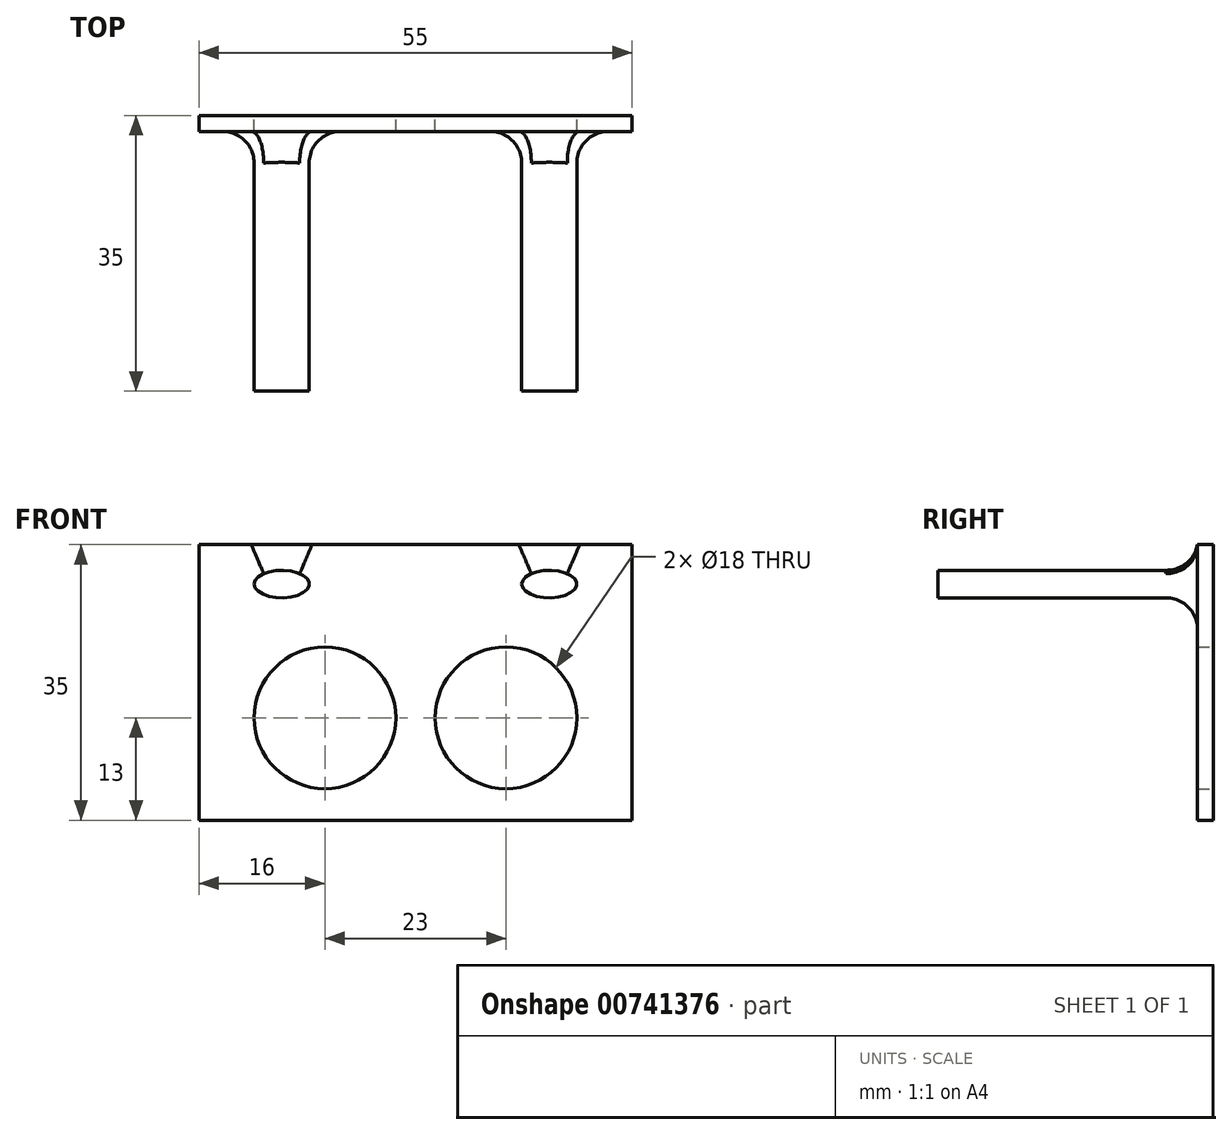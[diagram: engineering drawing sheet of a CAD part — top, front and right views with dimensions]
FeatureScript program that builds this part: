
annotation { "Feature Type Name" : "Feature", "Feature Type Description" : "" }
export const myFeature = defineFeature(function(context is Context, id is Id, definition is map)
    precondition{}
    {
        {
            var Q0;
            Q0=qCreatedBy(makeId("Front.planeOp"),FACE);
            var sketch = newSketch(context, id + "F0", { "sketchPlane" : qUnion([Q0])});
            skLineSegment(sketch, "E0.bottom", {"start": v(0, 0) * mm, "end": v(-55, 0) * mm});
            skLineSegment(sketch, "E0.top", {"start": v(0, -35) * mm, "end": v(-55, -35) * mm});
            skLineSegment(sketch, "E0.left", {"start": v(0, 0) * mm, "end": v(0, -35) * mm});
            skLineSegment(sketch, "E0.right", {"start": v(-55, 0) * mm, "end": v(-55, -35) * mm});
            skPoint(sketch, "E1", {"position": v(-39, -22) * mm});
            skPoint(sketch, "E2", {"position": v(-16, -22) * mm});
            skSolve(sketch);
        }
        {
            var Q0;
            Q0=makeQuery(id+"F0.imprint","IMPRINT",FACE,{"disambiguationData":[TD([[makeQuery(id+"F0.imprint","IMPRINT",EDGE,{"derivedFrom":sQuery(id+"F0.wireOp",EDGE,"E0.bottom")}),1.0]])]});
            extrude(context, id + "F1", {"entities" : qUnion([Q0]), "depth" : 2 * mm, "offsetDistance" : 25 * mm});
        }
        {
            var Q0;
            Q0=sQuery(id+"F0.wireOp",VERTEX,"E2");
            var Q1;
            Q1=sQuery(id+"F0.wireOp",VERTEX,"E1");
            var Q2;
            Q2=makeQuery(id+"F1.opExtrude","SWEPT_BODY",BODY,{"disambiguationData":[OSD([sQuery(id+"F0.wireOp",EDGE,"E0.bottom"),sQuery(id+"F0.wireOp",EDGE,"E0.top"),sQuery(id+"F0.wireOp",EDGE,"E0.left"),sQuery(id+"F0.wireOp",EDGE,"E0.right")])]});
            hole(context, id + "F2", {"style" : HoleStyle.SIMPLE, "endStyle" : HoleEndStyle.THROUGH, "oppositeDirection" : true, "holeDiameter" : 18 * mm, "majorDiameter" : 5 * mm, "isTappedThrough" : true, "tappedDepth" : 12 * mm, "tapClearance" : 3, "locations" : qUnion([Q0, Q1]), "scope" : qUnion([Q2])});
        }
        {
            var Q0;
            Q0=makeQuery(id+"F0.imprint","IMPRINT",FACE,{"disambiguationData":[TD([[makeQuery(id+"F0.imprint","IMPRINT",EDGE,{"derivedFrom":sQuery(id+"F0.wireOp",EDGE,"E0.bottom")}),1.0]])]});
            var sketch = newSketch(context, id + "F3", { "sketchPlane" : qUnion([Q0])});
            skPoint(sketch, "E3", {"position": v(-10.5, -5) * mm});
            skPoint(sketch, "E4", {"position": v(-44.5, -5) * mm});
            skEllipse(sketch, "E5", {"center": v(-10.5, -5) * mm, "majorRadius": 3.5 * mm, "minorRadius": 1.75 * mm, "majorAxis": v(-1, 0)});
            skEllipse(sketch, "E6", {"center": v(-44.5, -5) * mm, "majorRadius": 3.5 * mm, "minorRadius": 1.75 * mm, "majorAxis": v(-1, 0)});
            skSolve(sketch);
        }
        {
            var Q0;
            Q0 = qSketchRegion(id + "F3", true);
            extrude(context, id + "F4", {"entities" : qUnion([Q0]), "operationType" : NewBodyOperationType.ADD, "depth" : 35 * mm, "offsetDistance" : 25 * mm});
        }
        {
            var Q0;
            Q0=makeQuery(id+"F4.boolean.opBoolean","INTERSECT",EDGE,{"derivedFrom":[makeQuery(id+"F1.opExtrude","CAP_FACE",FACE,{"disambiguationData":[OSD([sQuery(id+"F0.wireOp",EDGE,"E0.bottom"),sQuery(id+"F0.wireOp",EDGE,"E0.top"),sQuery(id+"F0.wireOp",EDGE,"E0.left"),sQuery(id+"F0.wireOp",EDGE,"E0.right")])],"isStart":false}),makeQuery(id+"F4.opExtrude","SWEPT_FACE",FACE,{"disambiguationData":[OSD([sQuery(id+"F3.wireOp",EDGE,"E6")])]})]});
            var Q1;
            Q1=makeQuery(id+"F4.boolean.opBoolean","INTERSECT",EDGE,{"derivedFrom":[makeQuery(id+"F1.opExtrude","CAP_FACE",FACE,{"disambiguationData":[OSD([sQuery(id+"F0.wireOp",EDGE,"E0.bottom"),sQuery(id+"F0.wireOp",EDGE,"E0.top"),sQuery(id+"F0.wireOp",EDGE,"E0.left"),sQuery(id+"F0.wireOp",EDGE,"E0.right")])],"isStart":false}),makeQuery(id+"F4.opExtrude","SWEPT_FACE",FACE,{"disambiguationData":[OSD([sQuery(id+"F3.wireOp",EDGE,"E5")])]})]});
            fillet(context, id + "F5", {"entities" : qUnion([Q0, Q1]), "radius" : 4 * mm, "tangentPropagation" : true, "allowEdgeOverflow" : false});
        }
    });
